# Revit family: Sarlam_Eclairage_Hublot_Chartres_Infini_T1_Diam_300mm_1000Lm
name_source: partatom
category: Luminaires
units: mm (PartAtom-declared; Revit-internal decimal feet)

## family parameters
Cote de connecteur circulaire = Utiliser le diamètre
Couper avec des vides une fois chargée = Non
Hôte = Face
Partagée = Non
Point de calcul de pièce = Non
Source d'éclairage = Oui
Type d'élément = Normal

## types (12) — shared parameters
Adapté à un montage au plafond = Oui
Adapté à un montage en applique = Oui
Adapté à un montage en saillie = Oui
Adapté à un montage encastré = Non
Adapté à une suspension = Non
Angle de l'inclinaison = 0.00°
Angle du faisceau = Faisceau libre
Appareillage = Appareil à LED commandé en courant
Classe de protection = II
Condition Générale d'Utilisation = https://export.legrand.com
Diamètre externe = 300 mm  [stored 0.984252 ft]
Douille = Sans
Elévation par défaut = 2500 mm  [stored 8.2021 ft]
Emettre la visibilité des formes dans le rendu = Non
Emettre à partir du diamètre du cercle = 200 mm  [stored 0.656168 ft]
Fabricant = LEGRAND
Fichier de distribution photométrique = SL532000 .ies
Filtre de couleur = 16777215
Flux lumineux utile lm = 1000
Gradation des changements de température de couleur de lampe = <Aucun>
Hauteur/profondeur = 70 mm  [stored 0.229659 ft]
Indice de protection (IP) = IP55
Indice de protection contre les chocs (IK) = IK10
Indice de rendu des couleurs CRI = 80-89
Largeur = 300 mm  [stored 0.984252 ft]
Largeur d'encastrement = 300 mm  [stored 0.984252 ft]
Longueur = 300 mm  [stored 0.984252 ft]
Matériau du boîtier/corps = Plastique
Puissance de la lampe en Multiwatt = 14/24W
Répartition lumineuse = Symétrique
Source lumineuse = Led non interchangeable
Standard Formes 1-3-6 = Oui
Température de couleur K MAX = 4000
Température de couleur K MIN = 4000
Tension nominale (Un) V MAX = 253
Tension nominale (Un) V MIN = 207
Type de tension = CA
URL = http://www.legrandoc.com
zero-valued in all types: Diamètre d'encastrement, Hauteur/profondeur d'encastrement, Longueur d'encastrement

## per-type parameters (varying)
| type | Avec détecteur crépusculaire | Avec détecteur de mouvement | Couleur du boîtier/corps | Courant nominal mA MAX | Courant nominal mA MIN | Description | Modèle | Puissance du système W | Type de variation | Zone de détection |
| ON/OFF BLANC | Non | Non | LEGRAND - Blanc | 49 | 39 | CHARTRES INFINI 1000LM 4000K STANDARD ON/OFF BLANC | SL-532000 | 14 | Non régulable |  |
| ON/OFF ANTHRACITE | Non | Non | LEGRAND - Anthracite | 49 | 39 | CHARTRES INFINI 1000LM 4000K STANDARD ON/OFF ANTHRACITE | SL-532001 | 14 | Non régulable |  |
| ON/OFF GRIS METAL | Non | Non | LEGRAND - Gris métal | 49 | 39 | CHARTRES INFINI 1000LM 4000K STANDARD ON/OFF GRIS METAL | SL-532002 | 14 | Non régulable |  |
| Détection BLANC | Oui | Oui | LEGRAND - Blanc | 73 | 59 | CHARTRES INFINI 1000LM 4000K  STANDARD DETECTION HF BLANC | SL-532040 | 15 | Autre | Détection à 2,5m haut Plafond: Ø6m maxi Mur: Ellipse 16*17m |
| Détection ANTHRACITE | Oui | Oui | LEGRAND - Anthracite | 73 | 59 | CHARTRES INFINI 1000LM 4000K  STANDARD DETECTION HF ANTHRACITE | SL-532041 | 15 | Autre | Détection à 2,5m haut Plafond: Ø6m maxi Mur: Ellipse 16*17m |
| Détection GRIS METAL | Oui | Oui | LEGRAND - Gris métal | 73 | 59 | CHARTRES INFINI 1000LM 4000K  STANDARD DETECTION HF GRIS METAL | SL-532042 | 15 | Autre | Détection à 2,5m haut Plafond: Ø6m maxi Mur: Ellipse 16*17m |
| Détection+Horloge BLANC | Oui | Oui | LEGRAND - Blanc | 73 | 59 | CHARTRES INFINI 1000LM 4000K  STD DETECTION HF + HORLOGE BLANC | SL-532070 | 15 | Autre | Détection à 2,5m haut Plafond: Ø6m maxi Mur: Ellipse 16*17m |
| Détection+Horloge ANTHRACITE | Oui | Oui | LEGRAND - Anthracite | 73 | 59 | CHARTRES INFINI 1000LM 4000K  STD DETECTION HF + HORLOGE ANTHRACITE | SL-532071 | 15 | Autre | Détection à 2,5m haut Plafond: Ø6m maxi Mur: Ellipse 16*17m |
| Détection+Horloge GRIS METAL | Oui | Oui | LEGRAND - Gris métal | 73 | 59 | CHARTRES INFINI 1000LM 4000K  STD DETECTION HF + HORLOGE GRIS METAL | SL-532072 | 15 | Autre | Détection à 2,5m haut Plafond: Ø6m maxi Mur: Ellipse 16*17m |
| Double niveau/Minuterie BLANC | Non | Non | LEGRAND - Blanc | 73 | 59 | CHARTRES INFINI 1000LM 4000K STD DOUBLE NIVEAU/MINUTERIE BLANC | SL-532082 | 15 | Autre |  |
| Double niveau/Minuterie ANTHRACITE | Non | Non | LEGRAND - Anthracite | 73 | 59 | CHARTRES INFINI 1000LM 4000K STD DOUBLE NIVEAU/MINUTERIE ANTHRACITE | SL-532083 | 15 | Autre |  |
| Double niveau/Minuterie GRIS METAL | Non | Non | LEGRAND - Gris métal | 73 | 59 | CHARTRES INFINI 1000LM 4000K STD DOUBLE NIVEAU/MINUTERIE GRIS METAL | SL-532084 | 15 | Autre |  |

note: [stored X ft] marks values corroborated as IEEE doubles in the binary element streams (Revit-internal decimal feet)

## geometry (parser evidence)
native form markers: Blend x10
no freeform markers — native parametric forms only
